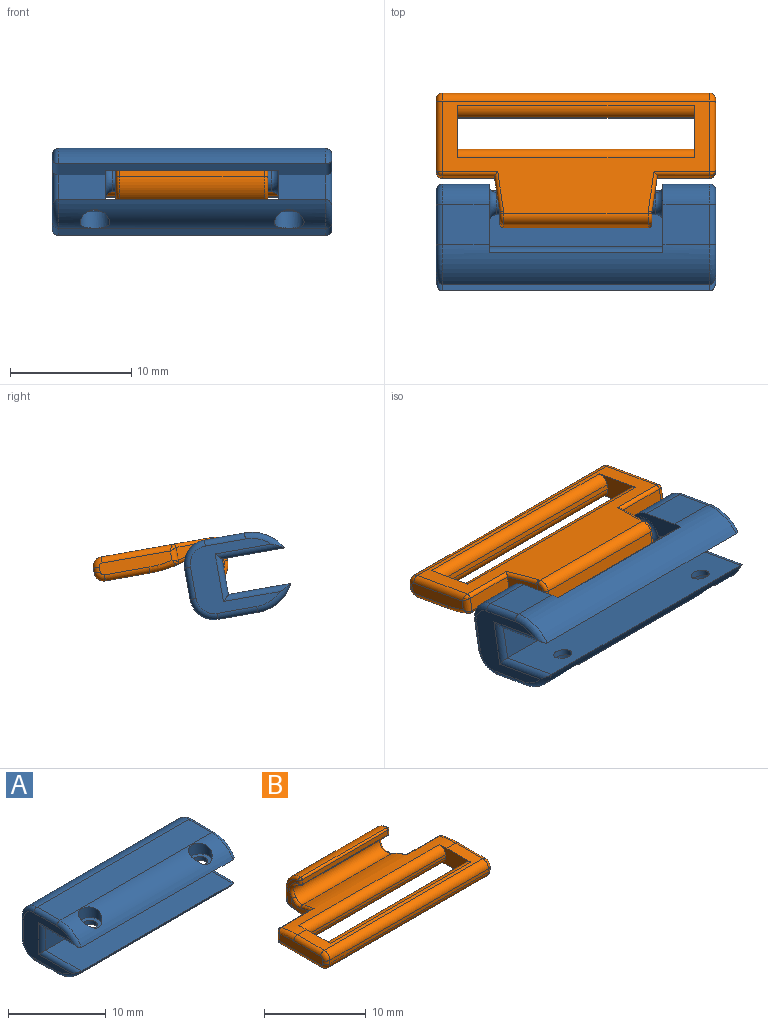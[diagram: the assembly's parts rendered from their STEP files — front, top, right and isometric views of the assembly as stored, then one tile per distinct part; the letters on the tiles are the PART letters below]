
ASSEMBLY  parts=2 mates=1
PART A: 49 faces, bbox 23x9.1x7.2 mm
  f0: plane 3.85x3.35mm, normal (0,0,-1), area 12.9mm2, adj f19,f22,f26,f37
  f1: plane 3.85x2.63mm, normal (0,1,0), area 10.1mm2, adj f18,f21,f23,f42
  f2: plane 22x5.22mm, normal (0,0,1), area 83.1mm2, adj f3,f10,f17,f18,f19,f26,f36,f47
  f3: plane 3.85x2.98mm, normal (0,-1,0), area 11.5mm2, adj f2,f9,f19,f34
  f4: plane 6.92x5.63mm, normal (1,0,0), area 18mm2, adj f29,f30,f31,f32,f33,f34,f35,f36
  f5: plane 6.92x5.63mm, normal (-1,0,0), area 18mm2, adj f39,f40,f41,f42,f43,f44,f45,f46
  f6: plane 3.85x2.63mm, normal (0,1,0), area 10.1mm2, adj f19,f22,f23,f33
  f7: plane 22x3.3mm, normal (0,0,1), area 72.7mm2, adj f23,f25,f29,f39
  f8: plane 3.85x3.35mm, normal (0,0,-1), area 12.9mm2, adj f18,f21,f26,f46
  f9: plane 22x8.4mm, normal (0,0,-1), area 156.7mm2, adj f3,f10,f11,f12,f18,f19,f23,f25
  f10: plane 3.85x2.98mm, normal (0,-1,0), area 11.5mm2, adj f2,f9,f18,f45
  f11: cylinder r=0.75mm len=1.5mm, axis (0,0,-1), area 2.4mm2, adj f9,f15
  f12: cylinder r=0.75mm len=1.5mm, axis (0,0,-1), area 2.4mm2, adj f9,f13
  f13: plane 2.45x2.45mm, normal (0,0,1), area 2.9mm2, adj f12,f14
  f14: cylinder r=1.22mm len=2.45mm, axis (0,0,-1), area 7.4mm2, adj f13,f25
  f15: plane 2.45x2.45mm, normal (0,0,1), area 2.9mm2, adj f11,f16
  f16: cylinder r=1.22mm len=2.45mm, axis (0,0,-1), area 7.4mm2, adj f15,f25
  f17: plane 14.3x0.78mm, normal (0,1,0), area 11.2mm2, adj f2,f18,f19,f24
  f18: plane 6.04x4.76mm, normal (1,0,0), area 11.4mm2, adj f1,f2,f8,f9,f10,f17,f21,f23
  f19: plane 6.04x4.76mm, normal (-1,0,0), area 11.4mm2, adj f0,f2,f3,f6,f9,f17,f22,f23
  f20: cylinder r=0.9mm len=13.1mm, axis (1,0,0), area 74.1mm2, adj f27,f28
  f21: cylinder r=2mm len=3.85mm, axis (-1,0,0), area 12.1mm2, adj f1,f8,f18,f44
  f22: cylinder r=2mm len=3.85mm, axis (-1,0,0), area 12.1mm2, adj f0,f6,f19,f35
  f23: cylinder r=2mm len=22mm, axis (1,0,0), area 67.3mm2, adj f1,f6,f7,f9,f18,f19,f31,f40
  f24: cylinder r=1mm len=14.3mm, axis (1,0,0), area 17.2mm2, adj f17,f18,f19,f26
  f25: cylinder r=3.5mm len=22mm, axis (1,0,0), area 73.1mm2, adj f7,f9,f14,f16,f30,f41
  f26: cylinder r=3.5mm len=22mm, axis (1,0,0), area 71.5mm2, adj f0,f2,f8,f18,f19,f24,f38,f48
  f27: torus R=1.5mm, axis (-1,0,0), area 6.6mm2, adj f19,f20
  f28: torus R=1.5mm, axis (-1,0,0), area 6.6mm2, adj f18,f20
  f29: cylinder r=0.5mm len=3.3mm, axis (0,-1,0), area 2.6mm2, adj f4,f7,f30,f31
  f30: torus R=3mm, axis (1,0,0), area 2.6mm2, adj f4,f25,f29,f32
  f31: torus R=1.5mm, axis (1,0,0), area 2.2mm2, adj f4,f23,f29,f33
  f32: cylinder r=0.5mm len=5.72mm, axis (0,1,0), area 4mm2, adj f4,f9,f30,f34
  f33: cylinder r=0.5mm len=2.63mm, axis (0,0,1), area 2.1mm2, adj f4,f6,f31,f35
  f34: cylinder r=0.5mm len=3.98mm, axis (0,0,-1), area 2.6mm2, adj f3,f4,f32,f36
  f35: torus R=1.5mm, axis (1,0,0), area 2.2mm2, adj f4,f22,f33,f37
  f36: cylinder r=0.5mm len=5.72mm, axis (0,-1,0), area 4mm2, adj f2,f4,f34,f38
  f37: cylinder r=0.5mm len=3.35mm, axis (0,1,0), area 2.6mm2, adj f0,f4,f35,f38
  f38: torus R=3mm, axis (1,0,0), area 2.5mm2, adj f4,f26,f36,f37
  f39: cylinder r=0.5mm len=3.3mm, axis (0,1,0), area 2.6mm2, adj f5,f7,f40,f41
  f40: torus R=1.5mm, axis (1,0,0), area 2.2mm2, adj f5,f23,f39,f42
  f41: torus R=3mm, axis (1,0,0), area 2.6mm2, adj f5,f25,f39,f43
  f42: cylinder r=0.5mm len=2.63mm, axis (0,0,-1), area 2.1mm2, adj f1,f5,f40,f44
  f43: cylinder r=0.5mm len=5.72mm, axis (0,-1,0), area 4mm2, adj f5,f9,f41,f45
  f44: torus R=1.5mm, axis (1,0,0), area 2.2mm2, adj f5,f21,f42,f46
  f45: cylinder r=0.5mm len=3.98mm, axis (0,0,1), area 2.6mm2, adj f5,f10,f43,f47
  f46: cylinder r=0.5mm len=3.35mm, axis (0,-1,0), area 2.6mm2, adj f5,f8,f44,f48
  f47: cylinder r=0.5mm len=5.72mm, axis (0,1,0), area 4mm2, adj f2,f5,f45,f48
  f48: torus R=3mm, axis (1,0,0), area 2.5mm2, adj f5,f26,f46,f47
PART B: 73 faces, bbox 23x11.2x4.3 mm
  f0: plane 11.9x1.3mm, normal (0,1,0), area 15.5mm2, adj f6,f20,f33,f46
  f1: plane 6x1mm, normal (1,0,0), area 5.8mm2, adj f55,f56,f57,f58,f59,f61,f62
  f2: plane 6x1mm, normal (-1,0,0), area 5.8mm2, adj f64,f65,f66,f67,f69,f70,f71
  f3: plane 22x9.4mm, normal (0,0,-1), area 89.2mm2, adj f6,f10,f11,f17,f18,f23,f29,f30
  f4: cylinder r=1.05mm len=12.36mm, axis (1,0,0), area 43.8mm2, adj f5,f21,f40,f41,f53,f54
  f5: cylinder r=10mm len=22mm, axis (1,0,0), area 53.1mm2, adj f4,f7,f10,f11,f16,f36,f38,f49
  f6: cylinder r=0.8mm len=11.9mm, axis (-1,0,0), area 15mm2, adj f0,f3,f32,f45
  f7: plane 22x3.72mm, normal (0,0,1), area 17.1mm2, adj f5,f10,f11,f19,f24,f56,f64
  f8: plane 22x0.4mm, normal (0,-1,0), area 8.8mm2, adj f23,f24,f57,f67
  f9: plane 19.5x0.4mm, normal (0,1,0), area 7.8mm2, adj f10,f11,f17,f19
  f10: plane 4.39x2mm, normal (1,0,0), area 6mm2, adj f3,f5,f7,f9,f12,f16,f17,f18
  f11: plane 4.39x2mm, normal (-1,0,0), area 6mm2, adj f3,f5,f7,f9,f12,f16,f17,f18
  f12: plane 19.5x0.35mm, normal (0,-1,0), area 6.8mm2, adj f10,f11,f16,f18
  f13: plane 11.9x0.55mm, normal (0,-1,0), area 6.6mm2, adj f21,f22,f37,f50
  f14: plane 3.5x1.51mm, normal (1,0,0), area 1.7mm2, adj f25,f44,f45,f46,f47,f50,f53,f54
  f15: plane 3.5x1.51mm, normal (-1,0,0), area 1.7mm2, adj f28,f31,f32,f33,f34,f37,f40,f41
  f16: cylinder r=0.8mm len=19.5mm, axis (1,0,0), area 26.2mm2, adj f5,f10,f11,f12
  f17: cylinder r=0.8mm len=19.5mm, axis (-1,0,0), area 24.5mm2, adj f3,f9,f10,f11
  f18: cylinder r=0.8mm len=19.5mm, axis (1,0,0), area 24.5mm2, adj f3,f10,f11,f12
  f19: cylinder r=0.8mm len=19.5mm, axis (-1,0,0), area 24.5mm2, adj f7,f9,f10,f11
  f20: cylinder r=2mm len=11.9mm, axis (1,0,0), area 36.1mm2, adj f0,f22,f34,f47
  f21: cylinder r=0.2mm len=11.9mm, axis (1,0,0), area 3.5mm2, adj f4,f13,f39,f52
  f22: cylinder r=0.2mm len=11.9mm, axis (1,0,0), area 3.9mm2, adj f13,f20,f35,f48
  f23: cylinder r=0.8mm len=22mm, axis (1,0,0), area 27.6mm2, adj f3,f8,f59,f69
  f24: cylinder r=0.8mm len=22mm, axis (-1,0,0), area 27.6mm2, adj f7,f8,f55,f65
  f25: plane 3.05x1.09mm, normal (0.99,0.14,0), area 2.1mm2, adj f14,f26,f43,f51,f53
  f26: plane 4.31x1.15mm, normal (0,1,0), area 5mm2, adj f25,f42,f49,f51,f62
  f27: plane 4.31x1.15mm, normal (0,1,0), area 5mm2, adj f28,f29,f36,f38,f70
  f28: plane 3.05x1.09mm, normal (-0.99,0.14,0), area 2.1mm2, adj f15,f27,f30,f38,f40
  f29: cylinder r=0.3mm len=4.57mm, axis (1,0,0), area 2.1mm2, adj f3,f27,f30,f72
  f30: cylinder r=0.3mm len=3.37mm, axis (0.14,0.99,0), area 1.5mm2, adj f3,f28,f29,f31
  f31: cylinder r=0.3mm len=0.3mm, axis (0,-1,0), area 0.1mm2, adj f3,f15,f30,f32
  f32: torus R=0.5mm, axis (-1,0,0), area 0.5mm2, adj f6,f15,f31,f33
  f33: cylinder r=0.3mm len=1.3mm, axis (0,0,1), area 0.6mm2, adj f0,f15,f32,f34
  f34: torus R=1.7mm, axis (-1,0,0), area 1.3mm2, adj f15,f20,f33,f35
  f35: bspline ~0.39x0.32mm, area 0.1mm2, adj f22,f34,f37
  f36: cylinder r=0.3mm len=4.57mm, axis (1,0,0), area 1.8mm2, adj f5,f27,f38,f68
  f37: cylinder r=0.3mm len=0.55mm, axis (0,0,-1), area 0.2mm2, adj f13,f15,f35,f39
  f38: bspline ~1.84x0.88mm, area 0.8mm2, adj f5,f27,f28,f36,f40
  f39: bspline ~0.38x0.3mm, area 0.1mm2, adj f21,f37,f41
  f40: bspline ~1.57x0.67mm, area 0.7mm2, adj f4,f15,f28,f38,f41
  f41: torus R=1.35mm, axis (-1,0,0), area 1.2mm2, adj f4,f15,f39,f40
  f42: cylinder r=0.3mm len=4.57mm, axis (1,0,0), area 2.1mm2, adj f3,f26,f43,f63
  f43: cylinder r=0.3mm len=3.37mm, axis (0.14,-0.99,0), area 1.5mm2, adj f3,f25,f42,f44
  f44: cylinder r=0.3mm len=0.3mm, axis (0,1,0), area 0.1mm2, adj f3,f14,f43,f45
  f45: torus R=0.5mm, axis (-1,0,0), area 0.5mm2, adj f6,f14,f44,f46
  f46: cylinder r=0.3mm len=1.3mm, axis (0,0,-1), area 0.6mm2, adj f0,f14,f45,f47
  f47: torus R=1.7mm, axis (-1,0,0), area 1.3mm2, adj f14,f20,f46,f48
  f48: bspline ~0.39x0.32mm, area 0.1mm2, adj f22,f47,f50
  f49: cylinder r=0.3mm len=4.57mm, axis (1,0,0), area 1.8mm2, adj f5,f26,f51,f60
  f50: cylinder r=0.3mm len=0.55mm, axis (0,0,1), area 0.2mm2, adj f13,f14,f48,f52
  f51: bspline ~1.84x0.88mm, area 0.8mm2, adj f5,f25,f26,f49,f53
  f52: bspline ~0.38x0.3mm, area 0.1mm2, adj f21,f50,f54
  f53: bspline ~1.57x0.67mm, area 0.7mm2, adj f4,f14,f25,f51,f54
  f54: torus R=1.35mm, axis (-1,0,0), area 1.2mm2, adj f4,f14,f52,f53
  f55: torus R=0.3mm, axis (1,0,0), area 0.8mm2, adj f1,f24,f56,f57
  f56: cylinder r=0.5mm len=3.72mm, axis (0,-1,0), area 2.9mm2, adj f1,f7,f55,f58
  f57: cylinder r=0.5mm len=0.5mm, axis (0,0,-1), area 0.3mm2, adj f1,f8,f55,f59
  f58: torus R=9.5mm, axis (1,0,0), area 1.7mm2, adj f1,f5,f56,f60
  f59: torus R=0.3mm, axis (1,0,0), area 0.8mm2, adj f1,f23,f57,f61
  f60: bspline ~0.63x0.5mm, area 0.1mm2, adj f49,f58,f62
  f61: cylinder r=0.5mm len=5.9mm, axis (0,1,0), area 4.6mm2, adj f1,f3,f59,f63
  f62: cylinder r=0.5mm len=1.15mm, axis (0,0,-1), area 0.8mm2, adj f1,f26,f60,f63
  f63: bspline ~0.6x0.5mm, area 0.2mm2, adj f42,f61,f62
  f64: cylinder r=0.5mm len=3.72mm, axis (0,1,0), area 2.9mm2, adj f2,f7,f65,f66
  f65: torus R=0.3mm, axis (1,0,0), area 0.8mm2, adj f2,f24,f64,f67
  f66: torus R=9.5mm, axis (1,0,0), area 1.7mm2, adj f2,f5,f64,f68
  f67: cylinder r=0.5mm len=0.5mm, axis (0,0,1), area 0.3mm2, adj f2,f8,f65,f69
  f68: bspline ~0.63x0.5mm, area 0.1mm2, adj f36,f66,f70
  f69: torus R=0.3mm, axis (1,0,0), area 0.8mm2, adj f2,f23,f67,f71
  f70: cylinder r=0.5mm len=1.15mm, axis (0,0,-1), area 0.8mm2, adj f2,f27,f68,f72
  f71: cylinder r=0.5mm len=5.9mm, axis (0,-1,0), area 4.6mm2, adj f2,f3,f69,f72
  f72: bspline ~0.53x0.5mm, area 0.2mm2, adj f29,f70,f71
PLACE A rot(axis=(0,-1,0.09),180deg) t=(5.21,9.37,12.54)mm
PLACE B rot(axis=(1,0,0),170deg) t=(5.19,15.39,11.58)mm
MATE cylindrical A.f27 <-> B.f20  axis (-1,0,0) through (5.21,11.58,10.12)mm
